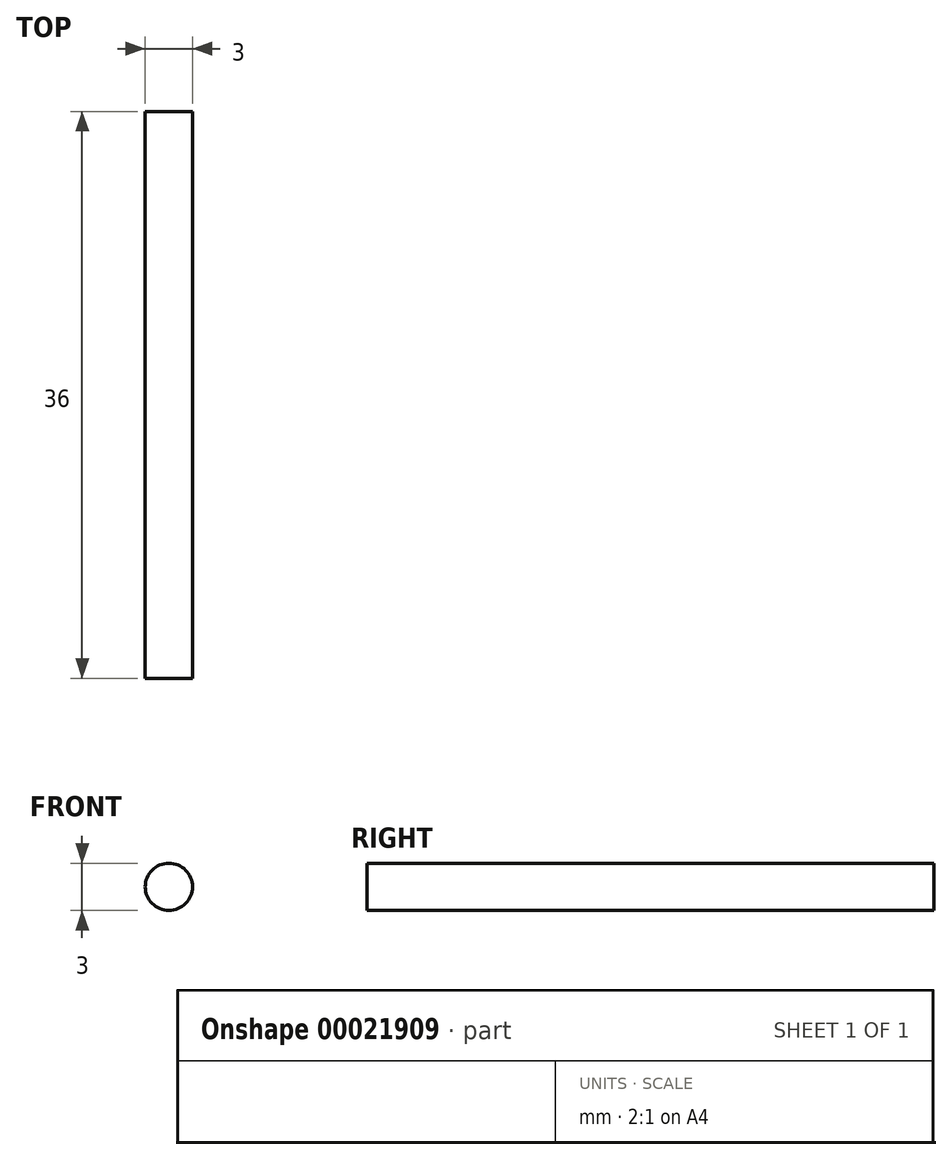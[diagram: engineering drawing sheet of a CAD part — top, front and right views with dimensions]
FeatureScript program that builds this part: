
annotation { "Feature Type Name" : "Feature", "Feature Type Description" : "" }
export const myFeature = defineFeature(function(context is Context, id is Id, definition is map)
    precondition{}
    {
        {
            var Q0;
            Q0=qCreatedBy(makeId("Front.planeOp"),FACE);
            var sketch = newSketch(context, id + "F0", { "sketchPlane" : qUnion([Q0])});
            skCircle(sketch, "E0", {"center": v(0, 0) * mm, "radius": 1.5 * mm});
            skSolve(sketch);
        }
        {
            var Q0;
            Q0=makeQuery(id+"F0.imprint","IMPRINT",FACE,{"disambiguationData":[TD([[makeQuery(id+"F0.imprint","IMPRINT",EDGE,{"derivedFrom":sQuery(id+"F0.wireOp",EDGE,"E0")}),1.0]])]});
            extrude(context, id + "F1", {"entities" : qUnion([Q0]), "depth" : 36 * mm});
        }
    });
